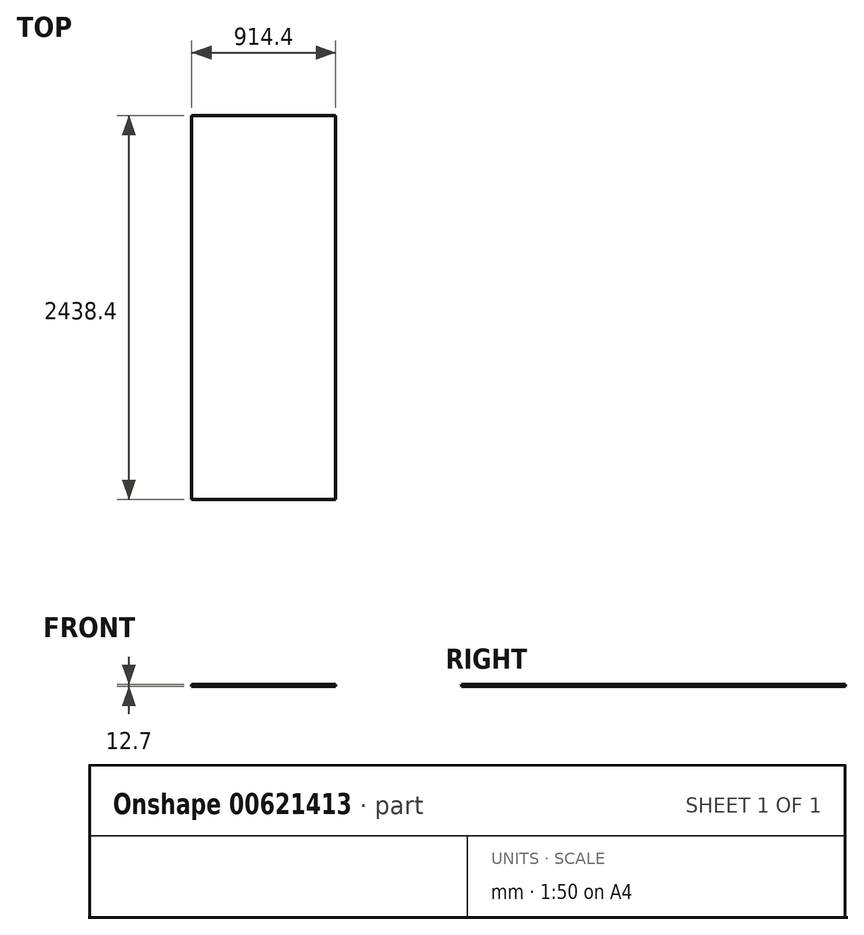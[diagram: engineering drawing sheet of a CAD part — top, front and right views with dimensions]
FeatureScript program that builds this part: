
annotation { "Feature Type Name" : "Feature", "Feature Type Description" : "" }
export const myFeature = defineFeature(function(context is Context, id is Id, definition is map)
    precondition{}
    {
        {
            var Q0;
            Q0=qCreatedBy(makeId("Top.planeOp"),FACE);
            var sketch = newSketch(context, id + "F0", { "sketchPlane" : qUnion([Q0])});
            skLineSegment(sketch, "E0.bottom", {"start": v(457.2, 1219.2) * mm, "end": v(-457.2, 1219.2) * mm});
            skLineSegment(sketch, "E0.top", {"start": v(457.2, -1219.2) * mm, "end": v(-457.2, -1219.2) * mm});
            skLineSegment(sketch, "E0.left", {"start": v(457.2, 1219.2) * mm, "end": v(457.2, -1219.2) * mm});
            skLineSegment(sketch, "E0.right", {"start": v(-457.2, 1219.2) * mm, "end": v(-457.2, -1219.2) * mm});
            skPoint(sketch, "E0.middle", {"position": v(0, 0) * mm});
            skSolve(sketch);
        }
        {
            var Q0;
            Q0 = qSketchRegion(id + "F0", true);
            extrude(context, id + "F1", {"entities" : qUnion([Q0]), "endBound" : BoundingType.SYMMETRIC, "depth" : 12.7 * mm, "offsetDistance" : 25.4 * mm});
        }
    });
